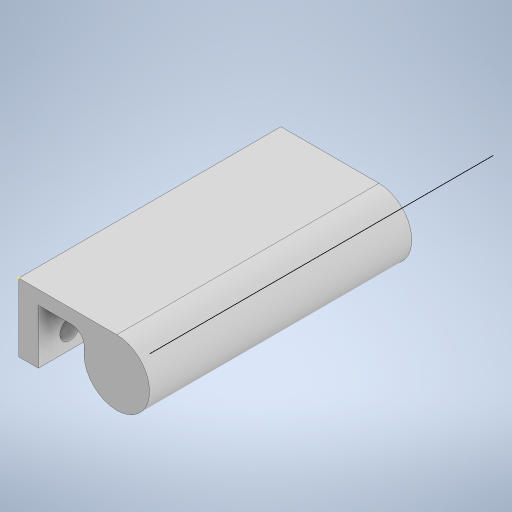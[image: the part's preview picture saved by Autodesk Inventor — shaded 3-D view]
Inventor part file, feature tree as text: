
AUTODESK INVENTOR PART (.ipt)
format: ipt  version: 2024.2 (Build 282272000, 272)  size: 267,776 bytes
history: native  units: in
note: dims shown in document units (in); Inventor stores cm internally (conversion verified against a paired STEP export)
features: sketch x4, extrude x3
ambient origin geometry x8: Origin, YZ Plane, XZ Plane, XY Plane, X Axis, Y Axis, Z Axis, Center Point
bodies: Solid1 (feature_tree)
feature tree (7):
  extrude  "Extrusion1"  Depth=0.65in
  extrude  "Extrusion2"  Depth=0.3937in
  extrude  "Extrusion3"  Depth=0.13in
  sketch  "Sketch4"  dims[d15=0.04in d16=0.0in d17=0.935in d18=0.625in d19=0.125in d20=2.5in d21=0.0in]
  sketch  "Sketch1"  dims[d0=2.5in d1=0.65in]
  sketch  "Sketch2"  dims[d4=2.7559in d6=0.3149in d7=0.3937in d9=1.0in d11=0.3in]
  sketch  "Sketch3"  dims[d12=0.1875in d13=0.0in d14=0.13in]
